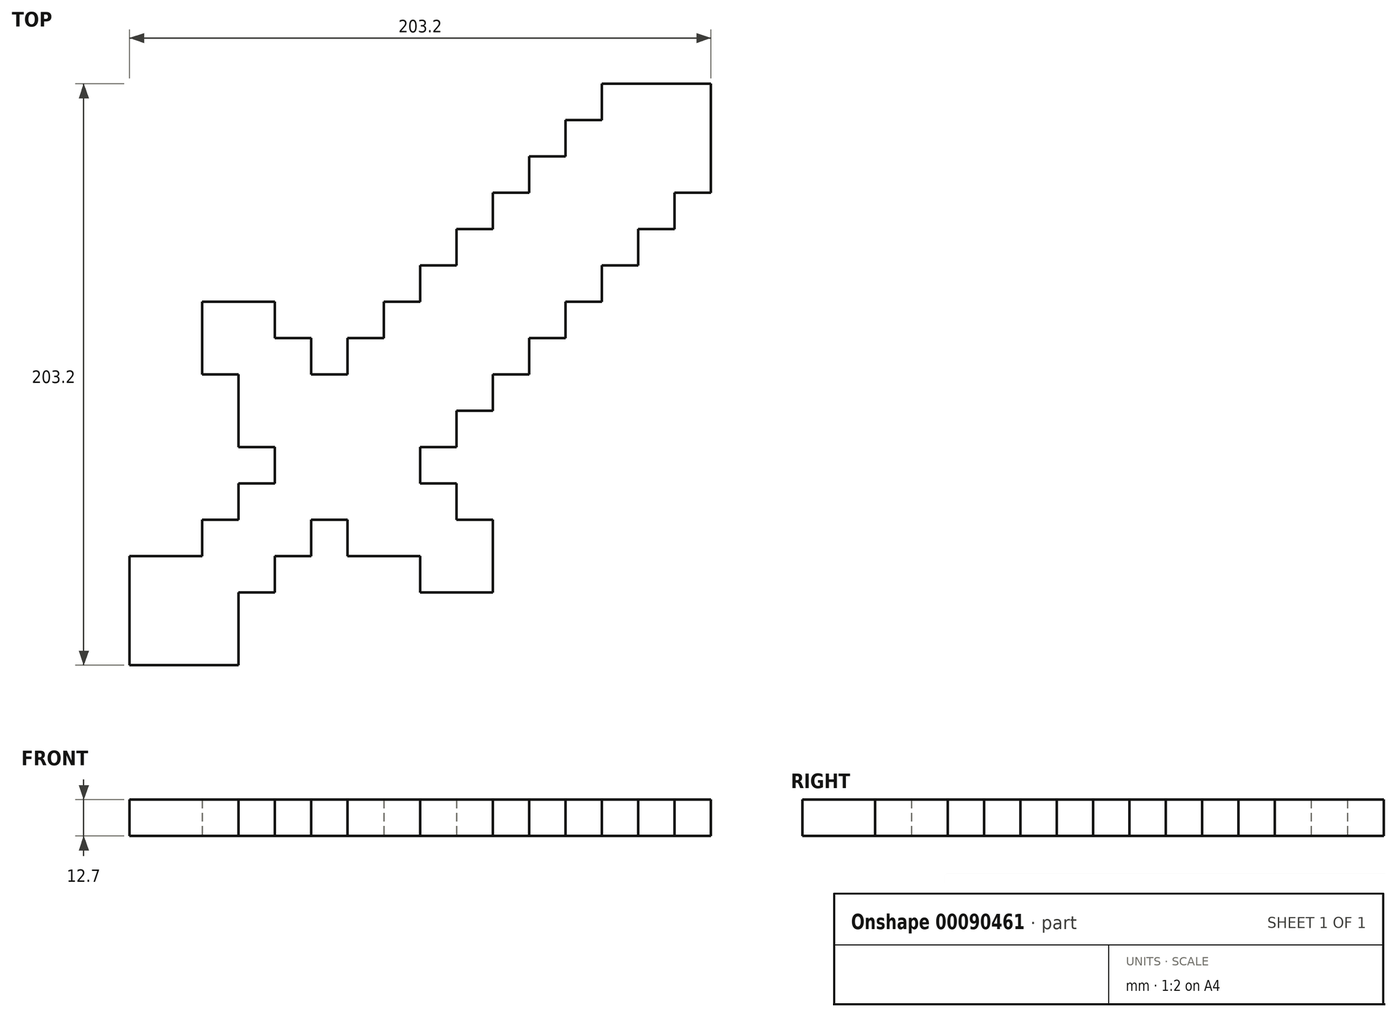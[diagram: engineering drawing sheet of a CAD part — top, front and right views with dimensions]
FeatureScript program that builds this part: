
annotation { "Feature Type Name" : "Feature", "Feature Type Description" : "" }
export const myFeature = defineFeature(function(context is Context, id is Id, definition is map)
    precondition{}
    {
        {
            var Q0;
            Q0=qCreatedBy(makeId("Top.planeOp"),FACE);
            var sketch = newSketch(context, id + "F0", { "sketchPlane" : qUnion([Q0])});
            skLineSegment(sketch, "E0.top", {"start": v(0, -101.6) * mm, "end": v(101.6, -101.6) * mm});
            skLineSegment(sketch, "E0.right", {"start": v(101.6, 0) * mm, "end": v(101.6, -101.6) * mm});
            skLineSegment(sketch, "E1.bottom", {"start": v(101.6, -101.6) * mm, "end": v(12.7, -101.6) * mm});
            skLineSegment(sketch, "E1.left", {"start": v(101.6, -101.6) * mm, "end": v(101.6, 101.6) * mm});
            skLineSegment(sketch, "E2", {"start": v(-101.6, 101.6) * mm, "end": v(-88.9, 101.6) * mm});
            skLineSegment(sketch, "E3", {"start": v(-88.9, 63.5) * mm, "end": v(-88.9, -50.8) * mm});
            skLineSegment(sketch, "E4", {"start": v(-88.9, 101.6) * mm, "end": v(-76.2, 101.6) * mm});
            skLineSegment(sketch, "E5", {"start": v(-76.2, 101.6) * mm, "end": v(-63.5, 101.6) * mm});
            skLineSegment(sketch, "E6", {"start": v(-63.5, 101.6) * mm, "end": v(-50.8, 101.6) * mm});
            skLineSegment(sketch, "E7", {"start": v(-25.4, 101.6) * mm, "end": v(-12.7, 101.6) * mm});
            skLineSegment(sketch, "E8", {"start": v(-12.7, 101.6) * mm, "end": v(0, 101.6) * mm});
            skLineSegment(sketch, "E9", {"start": v(0, 101.6) * mm, "end": v(12.7, 101.6) * mm});
            skLineSegment(sketch, "E10", {"start": v(12.7, 101.6) * mm, "end": v(25.4, 101.6) * mm});
            skLineSegment(sketch, "E11", {"start": v(25.4, 101.6) * mm, "end": v(38.1, 101.6) * mm});
            skLineSegment(sketch, "E12", {"start": v(38.1, 101.6) * mm, "end": v(50.8, 101.6) * mm});
            skLineSegment(sketch, "E13", {"start": v(63.5, 101.6) * mm, "end": v(76.2, 101.6) * mm});
            skLineSegment(sketch, "E14", {"start": v(76.2, 101.6) * mm, "end": v(88.9, 101.6) * mm});
            skLineSegment(sketch, "E15", {"start": v(88.9, 101.6) * mm, "end": v(101.6, 101.6) * mm});
            skLineSegment(sketch, "E16", {"start": v(-50.8, 101.6) * mm, "end": v(-38.1, 101.6) * mm});
            skLineSegment(sketch, "E17", {"start": v(-38.1, 101.6) * mm, "end": v(-25.4, 101.6) * mm});
            skLineSegment(sketch, "E18", {"start": v(-76.2, 63.5) * mm, "end": v(-76.2, 38.1) * mm});
            skLineSegment(sketch, "E19", {"start": v(-63.5, 101.6) * mm, "end": v(-63.5, 38.1) * mm});
            skLineSegment(sketch, "E20", {"start": v(-50.8, 101.6) * mm, "end": v(-50.8, 38.1) * mm});
            skLineSegment(sketch, "E21", {"start": v(-38.1, 101.6) * mm, "end": v(-38.1, 25.4) * mm});
            skLineSegment(sketch, "E22", {"start": v(-38.1, -101.6) * mm, "end": v(-38.1, -76.2) * mm});
            skLineSegment(sketch, "E23", {"start": v(-25.4, 101.6) * mm, "end": v(-25.4, 25.4) * mm});
            skLineSegment(sketch, "E24", {"start": v(-25.4, -101.6) * mm, "end": v(-25.4, -76.2) * mm});
            skLineSegment(sketch, "E25", {"start": v(-12.7, 101.6) * mm, "end": v(-12.7, 50.8) * mm});
            skLineSegment(sketch, "E26", {"start": v(-12.7, -101.6) * mm, "end": v(-12.7, -88.9) * mm});
            skLineSegment(sketch, "E27", {"start": v(0, 101.6) * mm, "end": v(0, 50.8) * mm});
            skLineSegment(sketch, "E28", {"start": v(12.7, 101.6) * mm, "end": v(12.7, 63.5) * mm});
            skLineSegment(sketch, "E29", {"start": v(12.7, -101.6) * mm, "end": v(12.7, -88.9) * mm});
            skLineSegment(sketch, "E30", {"start": v(25.4, -101.6) * mm, "end": v(25.4, -88.9) * mm});
            skLineSegment(sketch, "E31", {"start": v(38.1, -101.6) * mm, "end": v(38.1, -12.7) * mm});
            skLineSegment(sketch, "E32", {"start": v(50.8, -101.6) * mm, "end": v(50.8, 0) * mm});
            skLineSegment(sketch, "E33", {"start": v(63.5, 101.6) * mm, "end": v(63.5, 88.9) * mm});
            skLineSegment(sketch, "E34", {"start": v(63.5, -101.6) * mm, "end": v(63.5, 12.7) * mm});
            skLineSegment(sketch, "E35", {"start": v(76.2, -101.6) * mm, "end": v(76.2, 25.4) * mm});
            skLineSegment(sketch, "E36", {"start": v(88.9, -101.6) * mm, "end": v(101.6, -101.6) * mm});
            skLineSegment(sketch, "E37", {"start": v(-101.6, 76.2) * mm, "end": v(-101.6, 63.5) * mm});
            skLineSegment(sketch, "E38", {"start": v(-101.6, 63.5) * mm, "end": v(-101.6, 50.8) * mm});
            skLineSegment(sketch, "E39", {"start": v(-101.6, 50.8) * mm, "end": v(-101.6, 38.1) * mm});
            skLineSegment(sketch, "E40", {"start": v(-101.6, 38.1) * mm, "end": v(-101.6, 25.4) * mm});
            skLineSegment(sketch, "E41", {"start": v(-101.6, 25.4) * mm, "end": v(-101.6, 12.7) * mm});
            skLineSegment(sketch, "E42", {"start": v(-101.6, 12.7) * mm, "end": v(-101.6, 0) * mm});
            skLineSegment(sketch, "E43", {"start": v(-101.6, 0) * mm, "end": v(-101.6, -12.7) * mm});
            skLineSegment(sketch, "E44", {"start": v(-101.6, -12.7) * mm, "end": v(-101.6, -25.4) * mm});
            skLineSegment(sketch, "E45", {"start": v(-101.6, -25.4) * mm, "end": v(-101.6, -38.1) * mm});
            skLineSegment(sketch, "E46", {"start": v(-101.6, -38.1) * mm, "end": v(-101.6, -50.8) * mm});
            skLineSegment(sketch, "E47", {"start": v(-101.6, -63.5) * mm, "end": v(-101.6, -76.2) * mm});
            skLineSegment(sketch, "E48", {"start": v(-101.6, -76.2) * mm, "end": v(-101.6, -88.9) * mm});
            skLineSegment(sketch, "E49", {"start": v(-101.6, -88.9) * mm, "end": v(-101.6, -101.6) * mm});
            skLineSegment(sketch, "E50", {"start": v(-63.5, 88.9) * mm, "end": v(38.1, 88.9) * mm});
            skLineSegment(sketch, "E51", {"start": v(-101.6, 63.5) * mm, "end": v(12.7, 63.5) * mm});
            skLineSegment(sketch, "E52", {"start": v(-101.6, 50.8) * mm, "end": v(0, 50.8) * mm});
            skLineSegment(sketch, "E53", {"start": v(-101.6, 38.1) * mm, "end": v(-25.4, 38.1) * mm});
            skLineSegment(sketch, "E54", {"start": v(101.6, 38.1) * mm, "end": v(88.9, 38.1) * mm});
            skLineSegment(sketch, "E55", {"start": v(-101.6, 25.4) * mm, "end": v(-88.9, 25.4) * mm});
            skLineSegment(sketch, "E56", {"start": v(101.6, 25.4) * mm, "end": v(76.2, 25.4) * mm});
            skLineSegment(sketch, "E57", {"start": v(-101.6, 12.7) * mm, "end": v(-88.9, 12.7) * mm});
            skLineSegment(sketch, "E58", {"start": v(101.6, 12.7) * mm, "end": v(76.2, 12.7) * mm});
            skLineSegment(sketch, "E59", {"start": v(-101.6, -12.7) * mm, "end": v(-76.2, -12.7) * mm});
            skLineSegment(sketch, "E60", {"start": v(101.6, -12.7) * mm, "end": v(38.1, -12.7) * mm});
            skLineSegment(sketch, "E61", {"start": v(-101.6, -25.4) * mm, "end": v(-76.2, -25.4) * mm});
            skLineSegment(sketch, "E62", {"start": v(101.6, -25.4) * mm, "end": v(25.4, -25.4) * mm});
            skLineSegment(sketch, "E63", {"start": v(-101.6, -38.1) * mm, "end": v(-76.2, -38.1) * mm});
            skLineSegment(sketch, "E64", {"start": v(101.6, -38.1) * mm, "end": v(25.4, -38.1) * mm});
            skLineSegment(sketch, "E65", {"start": v(-101.6, -50.8) * mm, "end": v(-88.9, -50.8) * mm});
            skLineSegment(sketch, "E66", {"start": v(101.6, -50.8) * mm, "end": v(38.1, -50.8) * mm});
            skLineSegment(sketch, "E67", {"start": v(-101.6, -63.5) * mm, "end": v(-76.2, -63.5) * mm});
            skLineSegment(sketch, "E68", {"start": v(101.6, -63.5) * mm, "end": v(38.1, -63.5) * mm});
            skLineSegment(sketch, "E69", {"start": v(101.6, -76.2) * mm, "end": v(38.1, -76.2) * mm});
            skLineSegment(sketch, "E70", {"start": v(101.6, -88.9) * mm, "end": v(0, -88.9) * mm});
            skLineSegment(sketch, "E71.trimOffspring", {"start": v(-63.5, -101.6) * mm, "end": v(-101.6, -101.6) * mm});
            skLineSegment(sketch, "E72.trimOffspring", {"start": v(-50.8, -88.9) * mm, "end": v(-12.7, -88.9) * mm});
            skLineSegment(sketch, "E73.trimOffspring", {"start": v(-76.2, -50.8) * mm, "end": v(-76.2, -63.5) * mm});
            skLineSegment(sketch, "E74.trimOffspring", {"start": v(-76.2, -38.1) * mm, "end": v(-101.6, -38.1) * mm});
            skLineSegment(sketch, "E75.trimOffspring", {"start": v(-63.5, -38.1) * mm, "end": v(-63.5, -50.8) * mm});
            skLineSegment(sketch, "E76.trimOffspring", {"start": v(-88.9, -50.8) * mm, "end": v(-101.6, -50.8) * mm});
            skLineSegment(sketch, "E77.trimOffspring", {"start": v(-63.5, -38.1) * mm, "end": v(-50.8, -38.1) * mm});
            skLineSegment(sketch, "E78.trimOffspring", {"start": v(-76.2, -50.8) * mm, "end": v(-63.5, -50.8) * mm});
            skLineSegment(sketch, "E79.trimOffspring", {"start": v(-50.8, -88.9) * mm, "end": v(-50.8, -101.6) * mm});
            skLineSegment(sketch, "E80.trimOffspring", {"start": v(-76.2, -63.5) * mm, "end": v(-101.6, -63.5) * mm});
            skLineSegment(sketch, "E81", {"start": v(-50.8, -63.5) * mm, "end": v(-50.8, -76.2) * mm});
            skLineSegment(sketch, "E82.trimOffspring", {"start": v(-50.8, -76.2) * mm, "end": v(-63.5, -76.2) * mm});
            skLineSegment(sketch, "E83.trimOffspring", {"start": v(-38.1, -76.2) * mm, "end": v(-25.4, -76.2) * mm});
            skLineSegment(sketch, "E84.trimOffspring", {"start": v(-38.1, -63.5) * mm, "end": v(-38.1, -50.8) * mm});
            skLineSegment(sketch, "E85.trimOffspring", {"start": v(-25.4, -76.2) * mm, "end": v(-25.4, -101.6) * mm});
            skLineSegment(sketch, "E86.trimOffspring", {"start": v(-25.4, -63.5) * mm, "end": v(0, -63.5) * mm});
            skLineSegment(sketch, "E87.trimOffspring", {"start": v(-38.1, -76.2) * mm, "end": v(-38.1, -101.6) * mm});
            skLineSegment(sketch, "E88.trimOffspring", {"start": v(12.7, -50.8) * mm, "end": v(25.4, -50.8) * mm});
            skLineSegment(sketch, "E89.trimOffspring", {"start": v(-12.7, 12.7) * mm, "end": v(-12.7, 25.4) * mm});
            skLineSegment(sketch, "E90.trimOffspring", {"start": v(-50.8, -38.1) * mm, "end": v(-63.5, -38.1) * mm});
            skLineSegment(sketch, "E91.trimOffspring", {"start": v(0, -63.5) * mm, "end": v(0, -76.2) * mm});
            skLineSegment(sketch, "E92.trimOffspring", {"start": v(0, -38.1) * mm, "end": v(12.7, -38.1) * mm});
            skLineSegment(sketch, "E93.trimOffspring", {"start": v(25.4, -25.4) * mm, "end": v(101.6, -25.4) * mm});
            skLineSegment(sketch, "E94.trimOffspring", {"start": v(12.7, -38.1) * mm, "end": v(12.7, -50.8) * mm});
            skLineSegment(sketch, "E95.trimOffspring", {"start": v(38.1, -12.7) * mm, "end": v(101.6, -12.7) * mm});
            skLineSegment(sketch, "E96.trimOffspring", {"start": v(50.8, 0) * mm, "end": v(101.6, 0) * mm});
            skLineSegment(sketch, "E97.trimOffspring", {"start": v(25.4, -25.4) * mm, "end": v(25.4, -38.1) * mm});
            skLineSegment(sketch, "E98.trimOffspring", {"start": v(76.2, 0) * mm, "end": v(101.6, 0) * mm});
            skLineSegment(sketch, "E99.trimOffspring", {"start": v(-76.2, -25.4) * mm, "end": v(-101.6, -25.4) * mm});
            skLineSegment(sketch, "E100.trimOffspring", {"start": v(-50.8, -25.4) * mm, "end": v(-50.8, -38.1) * mm});
            skLineSegment(sketch, "E101", {"start": v(-63.5, -25.4) * mm, "end": v(-50.8, -25.4) * mm});
            skLineSegment(sketch, "E102.trimOffspring", {"start": v(-63.5, 76.2) * mm, "end": v(25.4, 76.2) * mm});
            skLineSegment(sketch, "E103", {"start": v(-25.4, -50.8) * mm, "end": v(-25.4, -63.5) * mm});
            skLineSegment(sketch, "E104.trimOffspring", {"start": v(0, -76.2) * mm, "end": v(25.4, -76.2) * mm});
            skLineSegment(sketch, "E105.trimOffspring", {"start": v(0, -88.9) * mm, "end": v(101.6, -88.9) * mm});
            skLineSegment(sketch, "E106.trimOffspring", {"start": v(-25.4, -76.2) * mm, "end": v(-38.1, -76.2) * mm});
            skLineSegment(sketch, "E107.trimOffspring", {"start": v(-38.1, -88.9) * mm, "end": v(-50.8, -88.9) * mm});
            skLineSegment(sketch, "E108.trimOffspring", {"start": v(-38.1, -101.6) * mm, "end": v(-50.8, -101.6) * mm});
            skLineSegment(sketch, "E109.trimOffspring", {"start": v(0, -88.9) * mm, "end": v(0, -101.6) * mm});
            skLineSegment(sketch, "E110.trimOffspring", {"start": v(12.7, -88.9) * mm, "end": v(12.7, -101.6) * mm});
            skLineSegment(sketch, "E111.trimOffspring", {"start": v(25.4, -88.9) * mm, "end": v(25.4, -101.6) * mm});
            skLineSegment(sketch, "E112.trimOffspring", {"start": v(25.4, -76.2) * mm, "end": v(25.4, -50.8) * mm});
            skLineSegment(sketch, "E113.trimOffspring", {"start": v(38.1, -76.2) * mm, "end": v(101.6, -76.2) * mm});
            skLineSegment(sketch, "E114.trimOffspring", {"start": v(38.1, -63.5) * mm, "end": v(101.6, -63.5) * mm});
            skLineSegment(sketch, "E115.trimOffspring", {"start": v(25.4, -76.2) * mm, "end": v(0, -76.2) * mm});
            skLineSegment(sketch, "E116.trimOffspring", {"start": v(38.1, -50.8) * mm, "end": v(101.6, -50.8) * mm});
            skLineSegment(sketch, "E117.trimOffspring", {"start": v(25.4, -50.8) * mm, "end": v(25.4, -63.5) * mm});
            skLineSegment(sketch, "E118.trimOffspring", {"start": v(25.4, -38.1) * mm, "end": v(101.6, -38.1) * mm});
            skLineSegment(sketch, "E119.trimOffspring", {"start": v(25.4, -38.1) * mm, "end": v(25.4, -25.4) * mm});
            skLineSegment(sketch, "E120.trimOffspring", {"start": v(25.4, -50.8) * mm, "end": v(12.7, -50.8) * mm});
            skLineSegment(sketch, "E121", {"start": v(0, -25.4) * mm, "end": v(0, -38.1) * mm});
            skLineSegment(sketch, "E122.trimOffspring", {"start": v(38.1, -12.7) * mm, "end": v(38.1, -101.6) * mm});
            skLineSegment(sketch, "E123.trimOffspring", {"start": v(50.8, 0) * mm, "end": v(50.8, -101.6) * mm});
            skLineSegment(sketch, "E124.trimOffspring", {"start": v(-12.7, 12.7) * mm, "end": v(-25.4, 12.7) * mm});
            skLineSegment(sketch, "E125.trimOffspring", {"start": v(88.9, 38.1) * mm, "end": v(88.9, -101.6) * mm});
            skLineSegment(sketch, "E126.trimOffspring", {"start": v(63.5, 12.7) * mm, "end": v(101.6, 12.7) * mm});
            skLineSegment(sketch, "E127.trimOffspring", {"start": v(63.5, 12.7) * mm, "end": v(63.5, -101.6) * mm});
            skLineSegment(sketch, "E128.trimOffspring", {"start": v(76.2, 25.4) * mm, "end": v(101.6, 25.4) * mm});
            skLineSegment(sketch, "E129.trimOffspring", {"start": v(76.2, 25.4) * mm, "end": v(76.2, -101.6) * mm});
            skLineSegment(sketch, "E130.trimOffspring", {"start": v(88.9, 50.8) * mm, "end": v(101.6, 50.8) * mm});
            skLineSegment(sketch, "E131.trimOffspring", {"start": v(88.9, 38.1) * mm, "end": v(101.6, 38.1) * mm});
            skLineSegment(sketch, "E132.trimOffspring", {"start": v(-76.2, -12.7) * mm, "end": v(-101.6, -12.7) * mm});
            skLineSegment(sketch, "E133.trimOffspring", {"start": v(-76.2, -12.7) * mm, "end": v(-76.2, -38.1) * mm});
            skLineSegment(sketch, "E134.trimOffspring", {"start": v(-76.2, 0) * mm, "end": v(-63.5, 0) * mm});
            skLineSegment(sketch, "E135.trimOffspring", {"start": v(-88.9, 12.7) * mm, "end": v(-101.6, 12.7) * mm});
            skLineSegment(sketch, "E136.trimOffspring", {"start": v(-76.2, 25.4) * mm, "end": v(-50.8, 25.4) * mm});
            skLineSegment(sketch, "E137.trimOffspring", {"start": v(-76.2, 25.4) * mm, "end": v(-76.2, 0) * mm});
            skLineSegment(sketch, "E138.trimOffspring", {"start": v(-88.9, 25.4) * mm, "end": v(-101.6, 25.4) * mm});
            skLineSegment(sketch, "E139.trimOffspring", {"start": v(-63.5, 0) * mm, "end": v(-63.5, -25.4) * mm});
            skLineSegment(sketch, "E140.trimOffspring", {"start": v(-50.8, 25.4) * mm, "end": v(-50.8, 12.7) * mm});
            skLineSegment(sketch, "E141.trimOffspring", {"start": v(-50.8, 25.4) * mm, "end": v(-76.2, 25.4) * mm});
            skLineSegment(sketch, "E142.trimOffspring", {"start": v(-38.1, 25.4) * mm, "end": v(-25.4, 25.4) * mm});
            skLineSegment(sketch, "E143.trimOffspring", {"start": v(-38.1, 12.7) * mm, "end": v(-38.1, 0) * mm});
            skLineSegment(sketch, "E144.trimOffspring", {"start": v(-38.1, 25.4) * mm, "end": v(-38.1, 101.6) * mm});
            skLineSegment(sketch, "E145.trimOffspring", {"start": v(-25.4, 12.7) * mm, "end": v(-12.7, 12.7) * mm});
            skLineSegment(sketch, "E146.trimOffspring", {"start": v(-25.4, 25.4) * mm, "end": v(-25.4, 101.6) * mm});
            skLineSegment(sketch, "E147.trimOffspring", {"start": v(-12.7, 25.4) * mm, "end": v(0, 25.4) * mm});
            skLineSegment(sketch, "E148.trimOffspring", {"start": v(-25.4, 25.4) * mm, "end": v(-38.1, 25.4) * mm});
            skLineSegment(sketch, "E149.trimOffspring", {"start": v(-12.7, 38.1) * mm, "end": v(-12.7, 101.6) * mm});
            skLineSegment(sketch, "E150.trimOffspring", {"start": v(-12.7, 38.1) * mm, "end": v(-101.6, 38.1) * mm});
            skLineSegment(sketch, "E151.trimOffspring", {"start": v(-12.7, 25.4) * mm, "end": v(-12.7, 12.7) * mm});
            skLineSegment(sketch, "E152.trimOffspring", {"start": v(0, 38.1) * mm, "end": v(12.7, 38.1) * mm});
            skLineSegment(sketch, "E153.trimOffspring", {"start": v(0, 38.1) * mm, "end": v(0, 25.4) * mm});
            skLineSegment(sketch, "E154.trimOffspring", {"start": v(0, 50.8) * mm, "end": v(-101.6, 50.8) * mm});
            skLineSegment(sketch, "E155.trimOffspring", {"start": v(12.7, 63.5) * mm, "end": v(12.7, 101.6) * mm});
            skLineSegment(sketch, "E156.trimOffspring", {"start": v(12.7, 50.8) * mm, "end": v(25.4, 50.8) * mm});
            skLineSegment(sketch, "E157.trimOffspring", {"start": v(12.7, 63.5) * mm, "end": v(-101.6, 63.5) * mm});
            skLineSegment(sketch, "E158.trimOffspring", {"start": v(25.4, 76.2) * mm, "end": v(25.4, 101.6) * mm});
            skLineSegment(sketch, "E159.trimOffspring", {"start": v(38.1, 88.9) * mm, "end": v(38.1, 101.6) * mm});
            skLineSegment(sketch, "E160.trimOffspring", {"start": v(38.1, 76.2) * mm, "end": v(38.1, 63.5) * mm});
            skLineSegment(sketch, "E161.trimOffspring", {"start": v(25.4, 76.2) * mm, "end": v(-63.5, 76.2) * mm});
            skLineSegment(sketch, "E162.trimOffspring", {"start": v(25.4, 63.5) * mm, "end": v(25.4, 50.8) * mm});
            skLineSegment(sketch, "E163", {"start": v(50.8, 88.9) * mm, "end": v(63.5, 88.9) * mm});
            skLineSegment(sketch, "E164", {"start": v(63.5, 88.9) * mm, "end": v(63.5, 101.6) * mm});
            skLineSegment(sketch, "E165", {"start": v(38.1, 76.2) * mm, "end": v(50.8, 76.2) * mm});
            skLineSegment(sketch, "E166.trimOffspring", {"start": v(50.8, 76.2) * mm, "end": v(50.8, 88.9) * mm});
            skLineSegment(sketch, "E167.trimOffspring", {"start": v(38.1, 63.5) * mm, "end": v(25.4, 63.5) * mm});
            skLineSegment(sketch, "E168.trimOffspring", {"start": v(88.9, 63.5) * mm, "end": v(101.6, 63.5) * mm});
            skLineSegment(sketch, "E169.trimOffspring", {"start": v(25.4, 50.8) * mm, "end": v(12.7, 50.8) * mm});
            skLineSegment(sketch, "E170.trimOffspring", {"start": v(38.1, 63.5) * mm, "end": v(38.1, 76.2) * mm});
            skLineSegment(sketch, "E171.trimOffspring", {"start": v(0, 25.4) * mm, "end": v(-12.7, 25.4) * mm});
            skLineSegment(sketch, "E172.trimOffspring", {"start": v(25.4, 50.8) * mm, "end": v(25.4, 63.5) * mm});
            skLineSegment(sketch, "E173.trimOffspring", {"start": v(12.7, 38.1) * mm, "end": v(12.7, 50.8) * mm});
            skLineSegment(sketch, "E174.trimOffspring", {"start": v(0, -63.5) * mm, "end": v(-25.4, -63.5) * mm});
            skLineSegment(sketch, "E175.trimOffspring", {"start": v(12.7, -50.8) * mm, "end": v(12.7, -38.1) * mm});
            skLineSegment(sketch, "E176", {"start": v(-25.4, 12.7) * mm, "end": v(-25.4, 0) * mm});
            skLineSegment(sketch, "E177.trimOffspring", {"start": v(-63.5, -50.8) * mm, "end": v(-76.2, -50.8) * mm});
            skLineSegment(sketch, "E178", {"start": v(-38.1, -50.8) * mm, "end": v(-25.4, -50.8) * mm});
            skLineSegment(sketch, "E179.trimOffspring", {"start": v(-50.8, -63.5) * mm, "end": v(-38.1, -63.5) * mm});
            skLineSegment(sketch, "E180.trimOffspring", {"start": v(-38.1, 0) * mm, "end": v(-25.4, 0) * mm});
            skLineSegment(sketch, "E181.trimOffspring", {"start": v(-50.8, 12.7) * mm, "end": v(-38.1, 12.7) * mm});
            skLineSegment(sketch, "E182.trimOffspring", {"start": v(-38.1, 0) * mm, "end": v(-38.1, 12.7) * mm});
            skLineSegment(sketch, "E183.trimOffspring", {"start": v(-63.5, -76.2) * mm, "end": v(-63.5, -101.6) * mm});
            skLineSegment(sketch, "E184.trimOffspring", {"start": v(-63.5, -76.2) * mm, "end": v(-50.8, -76.2) * mm});
            skLineSegment(sketch, "E185", {"start": v(12.7, -12.7) * mm, "end": v(12.7, -25.4) * mm});
            skLineSegment(sketch, "E186", {"start": v(0, -25.4) * mm, "end": v(25.4, -25.4) * mm});
            skLineSegment(sketch, "E187", {"start": v(38.1, -12.7) * mm, "end": v(12.7, -12.7) * mm});
            skLineSegment(sketch, "E188", {"start": v(25.4, 0) * mm, "end": v(25.4, -25.4) * mm});
            skLineSegment(sketch, "E189", {"start": v(38.1, 12.7) * mm, "end": v(38.1, -12.7) * mm});
            skLineSegment(sketch, "E190", {"start": v(50.8, 25.4) * mm, "end": v(50.8, 0) * mm});
            skLineSegment(sketch, "E191", {"start": v(63.5, 38.1) * mm, "end": v(63.5, 12.7) * mm});
            skLineSegment(sketch, "E192", {"start": v(76.2, 50.8) * mm, "end": v(76.2, 25.4) * mm});
            skLineSegment(sketch, "E193", {"start": v(25.4, 0) * mm, "end": v(50.8, 0) * mm});
            skLineSegment(sketch, "E194", {"start": v(63.5, 12.7) * mm, "end": v(38.1, 12.7) * mm});
            skLineSegment(sketch, "E195", {"start": v(76.2, 25.4) * mm, "end": v(50.8, 25.4) * mm});
            skLineSegment(sketch, "E196", {"start": v(88.9, 38.1) * mm, "end": v(63.5, 38.1) * mm});
            skLineSegment(sketch, "E197", {"start": v(76.2, 50.8) * mm, "end": v(88.9, 50.8) * mm});
            skLineSegment(sketch, "E198", {"start": v(88.9, 63.5) * mm, "end": v(88.9, 38.1) * mm});
            skSolve(sketch);
        }
        {
            var Q0;
            Q0=makeQuery(id+"F0.imprint","IMPRINT",FACE,{"disambiguationData":[TD([[makeQuery(id+"F0.imprint","IMPRINT",EDGE,{"derivedFrom":sQuery(id+"F0.wireOp",EDGE,"E13")}),-1.0]])]});
            extrude(context, id + "F1", {"entities" : qUnion([Q0]), "depth" : 12.7 * mm});
        }
    });
